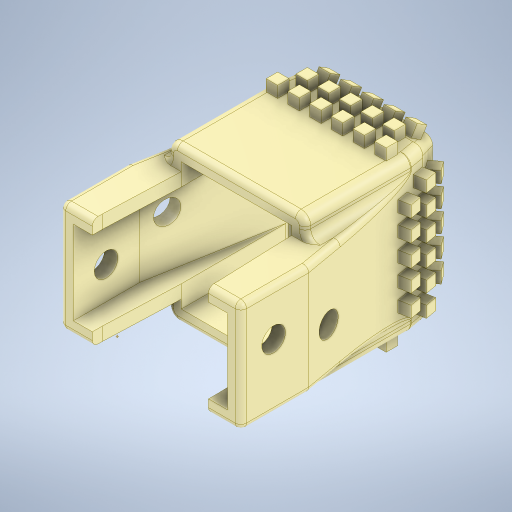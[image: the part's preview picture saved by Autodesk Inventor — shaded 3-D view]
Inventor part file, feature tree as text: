
AUTODESK INVENTOR PART (.ipt)
format: ipt  version: 2023.5 (Build 275446020, 446B)  size: 1,445,376 bytes
history: native  units: mm
features: other x27, extrude x18, fillet x3, mirror x2, loft x1, pattern_circular x1
ambient origin geometry x8: Origin, YZ Plane, XZ Plane, XY Plane, X Axis, Y Axis, Z Axis, Center Point
bodies: Solid1 (feature_tree)
feature tree (52):
  other  "NP2_Payload.ipt"
  other  "Sk:Params"
  extrude  "Ex:FrontSide"  Depth=10.0mm
  extrude  "Ex:FrontLip"  Depth=2.2mm
  other  "EndPlane"
  other  "SidePlane1"
  other  "Sk:EndCone"
  other  "Sk:MiddleLift"
  extrude  "Ex:MiddleLift"  TaperAngle=0.0deg  [1 undecoded]
  extrude  "Ex:FrontLift"  Depth=0.7mm
  loft  "Loft:EndCone"
  other  "FrontPlane"
  other  "SidePlane2"
  fillet  "Fillet:CircularEnd"  Radius=0.8mm
  other  "AnglePlane1"
  other  "Sk:AngleNub1"
  extrude  "Ex:AngleNub1-1"  TaperAngle=0.0deg  [1 undecoded]
  extrude  "Ex:AngleNub1-2"  Depth=0.2mm
  extrude  "Ex:AngleNub1-3"  TaperAngle=0.0deg  [1 undecoded]
  extrude  "Ex:AngleNub1-4"  Depth=0.7mm
  other  "AnglePlane2"
  other  "Sk:AngleNub2"
  extrude  "Ex:AngleNub2-1"  Depth=0.7mm
  extrude  "Ex:AngleNub2-2"  Depth=0.2mm
  extrude  "Ex:AngleNub2-3"  Depth=0.7mm
  extrude  "Ex:AngleNub2-4"  Depth=3.5mm
  extrude  "Ex:SideNub1"  TaperAngle=0.0deg  [1 undecoded]
  other  "Sk:SideNub2"
  extrude  "Ex:SideNub2"  Depth=0.2mm
  fillet  "Fillet:Cleanup"  Radius=0.7mm
  mirror  "Mirror1"
  mirror  "Mirror2"
  other  "SidePlane3"
  extrude  "Ex:UpperHole"  Depth=0.2mm
  extrude  "Ex:LowerHole"  Depth=20.0mm
  pattern_circular  "Pat:ReverseHoles"  Angle=360.0deg  [1 undecoded]
  fillet  "Fillet:Final"  Radius=1.25mm
  other  "SlicePlane1"
  other  "SlicePlane2"
  extrude  "Ex:Slice1"  Depth=0.3mm
  extrude  "Ex:Slice2"  TaperAngle=0.0deg  [1 undecoded]
  other  "TaggingFeature1"
  other  "Sk: Base"
  other  "Sk:FrontLip"
  other  "Sk:UpperHole"
  other  "Sk:LowerHole"
  other  "Sk:SideNub1"
  other  "Edges4"
  other  "Sk:Slice1"
  other  "Sk:Slice2"
  other  "Solid1::NP2_Payload.ipt"
  other  "Srf1"
note: 6 required parameter values undecoded (feature->parameter linkage not recoverable at this tier; creation-order binding heuristic only, values carry confidence <= 0.55)
